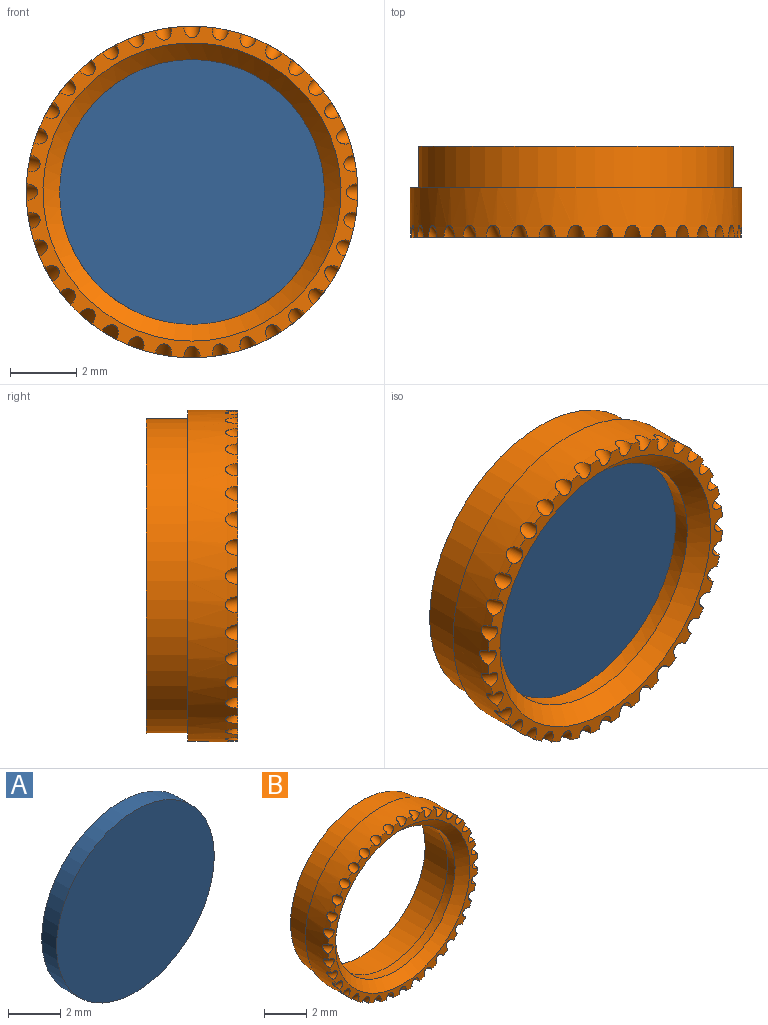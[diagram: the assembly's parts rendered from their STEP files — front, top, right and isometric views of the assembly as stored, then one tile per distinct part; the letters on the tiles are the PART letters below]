
ASSEMBLY  parts=2 mates=1
PART A: 3 faces, bbox 8.5x0.8x8.5 mm
  f0: plane 8.5x8.5mm, normal (0,-1,0), area 56.7mm2, adj f1
  f1: cylinder r=4.25mm len=8.5mm, axis (0,1,0), area 21.4mm2, adj f0,f2
  f2: plane 8.5x8.5mm, normal (0,1,0), area 56.7mm2, adj f1
PART B: 45 faces, bbox 10.4x2.9x10.4 mm
  f0: cylinder r=4.75mm len=9.5mm, axis (0,1,0), area 37.3mm2, adj f1,f7
  f1: plane 9.5x9.5mm, normal (0,1,0), area 14.1mm2, adj f0,f2
  f2: cylinder r=4.25mm len=8.5mm, axis (0,1,0), area 46.7mm2, adj f1,f3
  f3: plane 8.5x8.5mm, normal (0,1,0), area 6.5mm2, adj f2,f4
  f4: cylinder r=4mm len=8mm, axis (0,1,0), area 12.6mm2, adj f3,f8
  f5: plane 9.99x9.99mm, normal (0,-1,0), area 10.1mm2, adj f6,f8,f9,f10,f11,f12,f13,f14
  f6: cylinder r=5mm len=10mm, axis (0,1,0), area 42mm2, adj f5,f7,f9,f10,f11,f12,f13,f14
  f7: plane 10x10mm, normal (0,1,0), area 7.7mm2, adj f0,f6
  f8: cone r=4.5mm half-angle=45deg, axis (0,-1,0), area 18.9mm2, adj f4,f5
  f9: cylinder r=0.25mm len=0.53mm, axis (0,-0.73,-0.68), area 0.2mm2, adj f5,f6
  f10: cylinder r=0.25mm len=0.56mm, axis (-0.12,-0.73,-0.67), area 0.2mm2, adj f5,f6
  f11: cylinder r=0.25mm len=0.6mm, axis (-0.23,-0.73,-0.64), area 0.2mm2, adj f5,f6
  f12: cylinder r=0.25mm len=0.62mm, axis (-0.34,-0.73,-0.59), area 0.2mm2, adj f5,f6
  f13: cylinder r=0.25mm len=0.63mm, axis (-0.44,-0.73,-0.52), area 0.2mm2, adj f5,f6
  f14: cylinder r=0.25mm len=0.63mm, axis (-0.52,-0.73,-0.44), area 0.2mm2, adj f5,f6
  f15: cylinder r=0.25mm len=0.62mm, axis (-0.59,-0.73,-0.34), area 0.2mm2, adj f5,f6
  f16: cylinder r=0.25mm len=0.6mm, axis (-0.64,-0.73,-0.23), area 0.2mm2, adj f5,f6
  f17: cylinder r=0.25mm len=0.56mm, axis (-0.67,-0.73,-0.12), area 0.2mm2, adj f5,f6
  f18: cylinder r=0.25mm len=0.53mm, axis (-0.68,-0.73,0), area 0.2mm2, adj f5,f6
  f19: cylinder r=0.25mm len=0.56mm, axis (-0.67,-0.73,0.12), area 0.2mm2, adj f5,f6
  f20: cylinder r=0.25mm len=0.6mm, axis (-0.64,-0.73,0.23), area 0.2mm2, adj f5,f6
  f21: cylinder r=0.25mm len=0.62mm, axis (-0.59,-0.73,0.34), area 0.2mm2, adj f5,f6
  f22: cylinder r=0.25mm len=0.63mm, axis (-0.52,-0.73,0.44), area 0.2mm2, adj f5,f6
  f23: cylinder r=0.25mm len=0.63mm, axis (-0.44,-0.73,0.52), area 0.2mm2, adj f5,f6
  f24: cylinder r=0.25mm len=0.62mm, axis (-0.34,-0.73,0.59), area 0.2mm2, adj f5,f6
  f25: cylinder r=0.25mm len=0.6mm, axis (-0.23,-0.73,0.64), area 0.2mm2, adj f5,f6
  f26: cylinder r=0.25mm len=0.56mm, axis (-0.12,-0.73,0.67), area 0.2mm2, adj f5,f6
  f27: cylinder r=0.25mm len=0.53mm, axis (0,-0.73,0.68), area 0.2mm2, adj f5,f6
  f28: cylinder r=0.25mm len=0.56mm, axis (0.12,-0.73,0.67), area 0.2mm2, adj f5,f6
  f29: cylinder r=0.25mm len=0.6mm, axis (0.23,-0.73,0.64), area 0.2mm2, adj f5,f6
  f30: cylinder r=0.25mm len=0.62mm, axis (0.34,-0.73,0.59), area 0.2mm2, adj f5,f6
  f31: cylinder r=0.25mm len=0.63mm, axis (0.44,-0.73,0.52), area 0.2mm2, adj f5,f6
  f32: cylinder r=0.25mm len=0.63mm, axis (0.52,-0.73,0.44), area 0.2mm2, adj f5,f6
  f33: cylinder r=0.25mm len=0.62mm, axis (0.59,-0.73,0.34), area 0.2mm2, adj f5,f6
  f34: cylinder r=0.25mm len=0.6mm, axis (0.64,-0.73,0.23), area 0.2mm2, adj f5,f6
  f35: cylinder r=0.25mm len=0.56mm, axis (0.67,-0.73,0.12), area 0.2mm2, adj f5,f6
  f36: cylinder r=0.25mm len=0.53mm, axis (0.68,-0.73,0), area 0.2mm2, adj f5,f6
  f37: cylinder r=0.25mm len=0.56mm, axis (0.67,-0.73,-0.12), area 0.2mm2, adj f5,f6
  f38: cylinder r=0.25mm len=0.6mm, axis (0.64,-0.73,-0.23), area 0.2mm2, adj f5,f6
  f39: cylinder r=0.25mm len=0.62mm, axis (0.59,-0.73,-0.34), area 0.2mm2, adj f5,f6
  f40: cylinder r=0.25mm len=0.63mm, axis (0.52,-0.73,-0.44), area 0.2mm2, adj f5,f6
  f41: cylinder r=0.25mm len=0.63mm, axis (0.44,-0.73,-0.52), area 0.2mm2, adj f5,f6
  f42: cylinder r=0.25mm len=0.62mm, axis (0.34,-0.73,-0.59), area 0.2mm2, adj f5,f6
  f43: cylinder r=0.25mm len=0.6mm, axis (0.23,-0.73,-0.64), area 0.2mm2, adj f5,f6
  f44: cylinder r=0.25mm len=0.56mm, axis (0.12,-0.73,-0.67), area 0.2mm2, adj f5,f6
PLACE A at identity
PLACE B at identity
MATE fastened B.f0 <-> A.f1  axis (0,1,0) through (38,-15,59)mm
